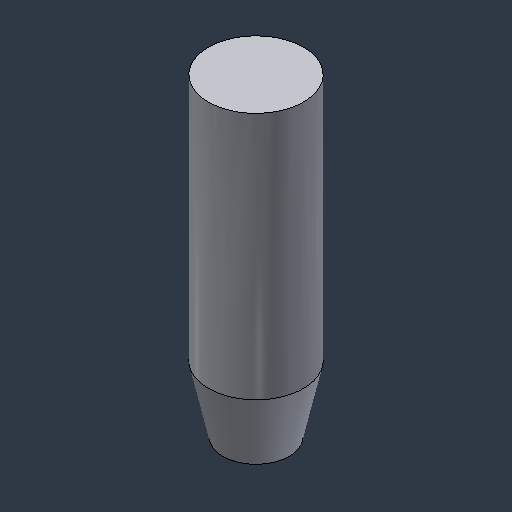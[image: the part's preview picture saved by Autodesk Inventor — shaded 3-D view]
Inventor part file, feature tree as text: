
AUTODESK INVENTOR PART (.ipt)
format: ipt  version: 2024.3 (Build 283343000, 343)  size: 88,576 bytes
history: native  units: mm (DEFAULTED — no unit token found)
features: chamfer x1
ambient origin geometry x8: Origin, YZ Plane, XZ Plane, XY Plane, X Axis, Y Axis, Z Axis, Center Point
bodies: Solid1 (feature_tree)
feature tree (1):
  chamfer  "Chamfer1"  [1 undecoded]
note: 1 required parameter value undecoded (feature->parameter linkage not recoverable at this tier; creation-order binding heuristic only, values carry confidence <= 0.55)
